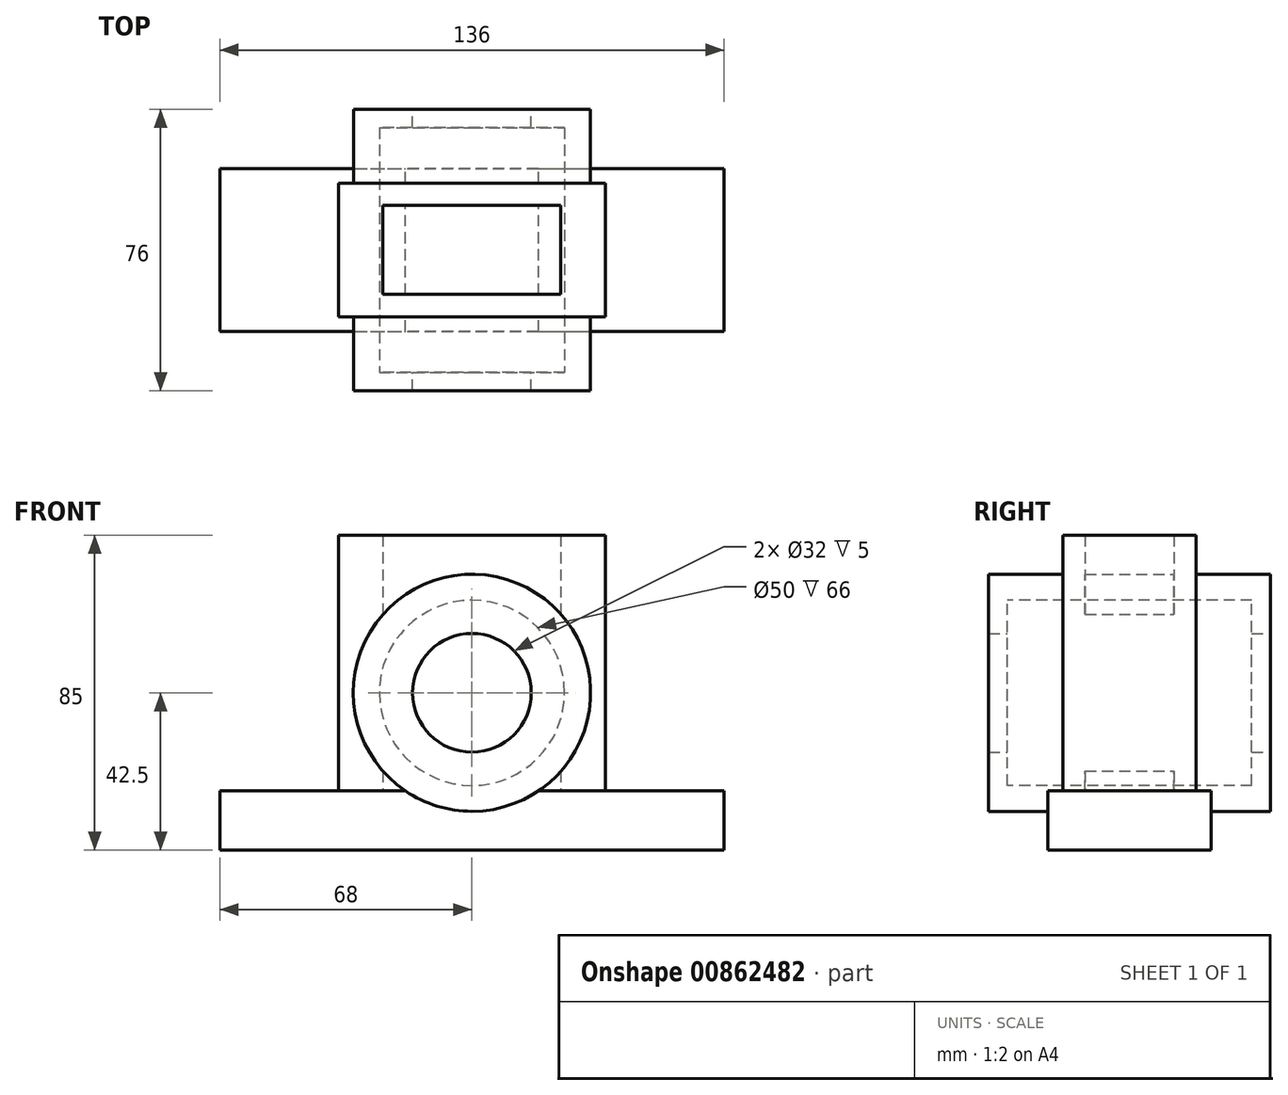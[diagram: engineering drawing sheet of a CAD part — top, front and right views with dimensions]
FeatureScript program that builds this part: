
annotation { "Feature Type Name" : "Feature", "Feature Type Description" : "" }
export const myFeature = defineFeature(function(context is Context, id is Id, definition is map)
    precondition{}
    {
        {
            var Q0;
            Q0=qCreatedBy(makeId("Front.planeOp"),FACE);
            var sketch = newSketch(context, id + "F0", { "sketchPlane" : qUnion([Q0])});
            skCircle(sketch, "E0", {"center": v(0, 0) * mm, "radius": 16 * mm});
            skCircle(sketch, "E1", {"center": v(0, 0) * mm, "radius": 32 * mm});
            skSolve(sketch);
        }
        {
            var Q0;
            Q0=makeQuery(id+"F0.imprint","IMPRINT",FACE,{"disambiguationData":[TD([[makeQuery(id+"F0.imprint","IMPRINT",EDGE,{"derivedFrom":sQuery(id+"F0.wireOp",EDGE,"E0")}),-1.0]])]});
            extrude(context, id + "F1", {"entities" : qUnion([Q0]), "endBound" : BoundingType.SYMMETRIC, "depth" : 76 * mm, "offsetDistance" : 25 * mm});
        }
        {
            var Q0;
            Q0=qCreatedBy(makeId("Top.planeOp"),FACE);
            var sketch = newSketch(context, id + "F2", { "sketchPlane" : qUnion([Q0])});
            skLineSegment(sketch, "E2.bottom", {"start": v(-36, 18) * mm, "end": v(36, 18) * mm});
            skLineSegment(sketch, "E2.top", {"start": v(-36, -18) * mm, "end": v(36, -18) * mm});
            skLineSegment(sketch, "E2.left", {"start": v(-36, 18) * mm, "end": v(-36, -18) * mm});
            skLineSegment(sketch, "E2.right", {"start": v(36, 18) * mm, "end": v(36, -18) * mm});
            skLineSegment(sketch, "E3.bottom", {"start": v(-24, 12) * mm, "end": v(24, 12) * mm});
            skLineSegment(sketch, "E3.top", {"start": v(-24, -12) * mm, "end": v(24, -12) * mm});
            skLineSegment(sketch, "E3.left", {"start": v(-24, 12) * mm, "end": v(-24, -12) * mm});
            skLineSegment(sketch, "E3.right", {"start": v(24, 12) * mm, "end": v(24, -12) * mm});
            skLineSegment(sketch, "E4", {"start": v(0, 0) * mm, "end": v(0, 34.48) * mm});
            skSolve(sketch);
        }
        {
            var Q0;
            Q0 = qSketchRegion(id + "F2", true);
            extrude(context, id + "F3", {"entities" : qUnion([Q0]), "operationType" : NewBodyOperationType.ADD, "endBound" : BoundingType.SYMMETRIC, "depth" : 85 * mm, "offsetDistance" : 25 * mm});
        }
        {
            var Q0;
            Q0=makeQuery(id+"F3.boolean.opBoolean","SPLIT",FACE,{"disambiguationData":[TD([makeQuery(id+"F1.opExtrude","SWEPT_FACE",FACE,{"disambiguationData":[OSD([sQuery(id+"F0.wireOp",EDGE,"E0")])]})])],"derivedFrom":makeQuery(id+"F3.opExtrude","SWEPT_FACE",FACE,{"disambiguationData":[OSD([sQuery(id+"F2.wireOp",EDGE,"E2.top")])]})});
            extrude(context, id + "F4", {"entities" : qUnion([Q0]), "operationType" : NewBodyOperationType.REMOVE, "endBound" : BoundingType.THROUGH_ALL, "oppositeDirection" : true, "depth" : 25 * mm, "offsetDistance" : 25 * mm});
        }
        {
            var Q0;
            Q0=makeQuery(id+"F3.opExtrude","CAP_FACE",FACE,{"disambiguationData":[OSD([sQuery(id+"F2.wireOp",EDGE,"E2.bottom"),sQuery(id+"F2.wireOp",EDGE,"E2.top"),sQuery(id+"F2.wireOp",EDGE,"E2.left"),sQuery(id+"F2.wireOp",EDGE,"E2.right"),sQuery(id+"F2.wireOp",EDGE,"E3.bottom"),sQuery(id+"F2.wireOp",EDGE,"E3.top"),sQuery(id+"F2.wireOp",EDGE,"E3.left"),sQuery(id+"F2.wireOp",EDGE,"E3.right")])],"isStart":true});
            var sketch = newSketch(context, id + "F5", { "sketchPlane" : qUnion([Q0])});
            skLineSegment(sketch, "E5.bottom", {"start": v(-68, 22) * mm, "end": v(68, 22) * mm});
            skLineSegment(sketch, "E5.top", {"start": v(-68, -22) * mm, "end": v(68, -22) * mm});
            skLineSegment(sketch, "E5.left", {"start": v(-68, 22) * mm, "end": v(-68, -22) * mm});
            skLineSegment(sketch, "E5.right", {"start": v(68, 22) * mm, "end": v(68, -22) * mm});
            skSolve(sketch);
        }
        {
            var Q0;
            Q0 = qSketchRegion(id + "F5", true);
            extrude(context, id + "F6", {"entities" : qUnion([Q0]), "operationType" : NewBodyOperationType.ADD, "oppositeDirection" : true, "depth" : 16 * mm, "offsetDistance" : 25 * mm});
        }
        {
            var Q0;
            Q0=qCreatedBy(makeId("Front.planeOp"),FACE);
            var sketch = newSketch(context, id + "F7", { "sketchPlane" : qUnion([Q0])});
            skCircle(sketch, "E6", {"center": v(0, 0) * mm, "radius": 25 * mm});
            skSolve(sketch);
        }
        {
            var Q0;
            Q0 = qSketchRegion(id + "F7", true);
            extrude(context, id + "F8", {"entities" : qUnion([Q0]), "operationType" : NewBodyOperationType.REMOVE, "endBound" : BoundingType.SYMMETRIC, "oppositeDirection" : true, "depth" : 66 * mm, "offsetDistance" : 25 * mm});
        }
    });
